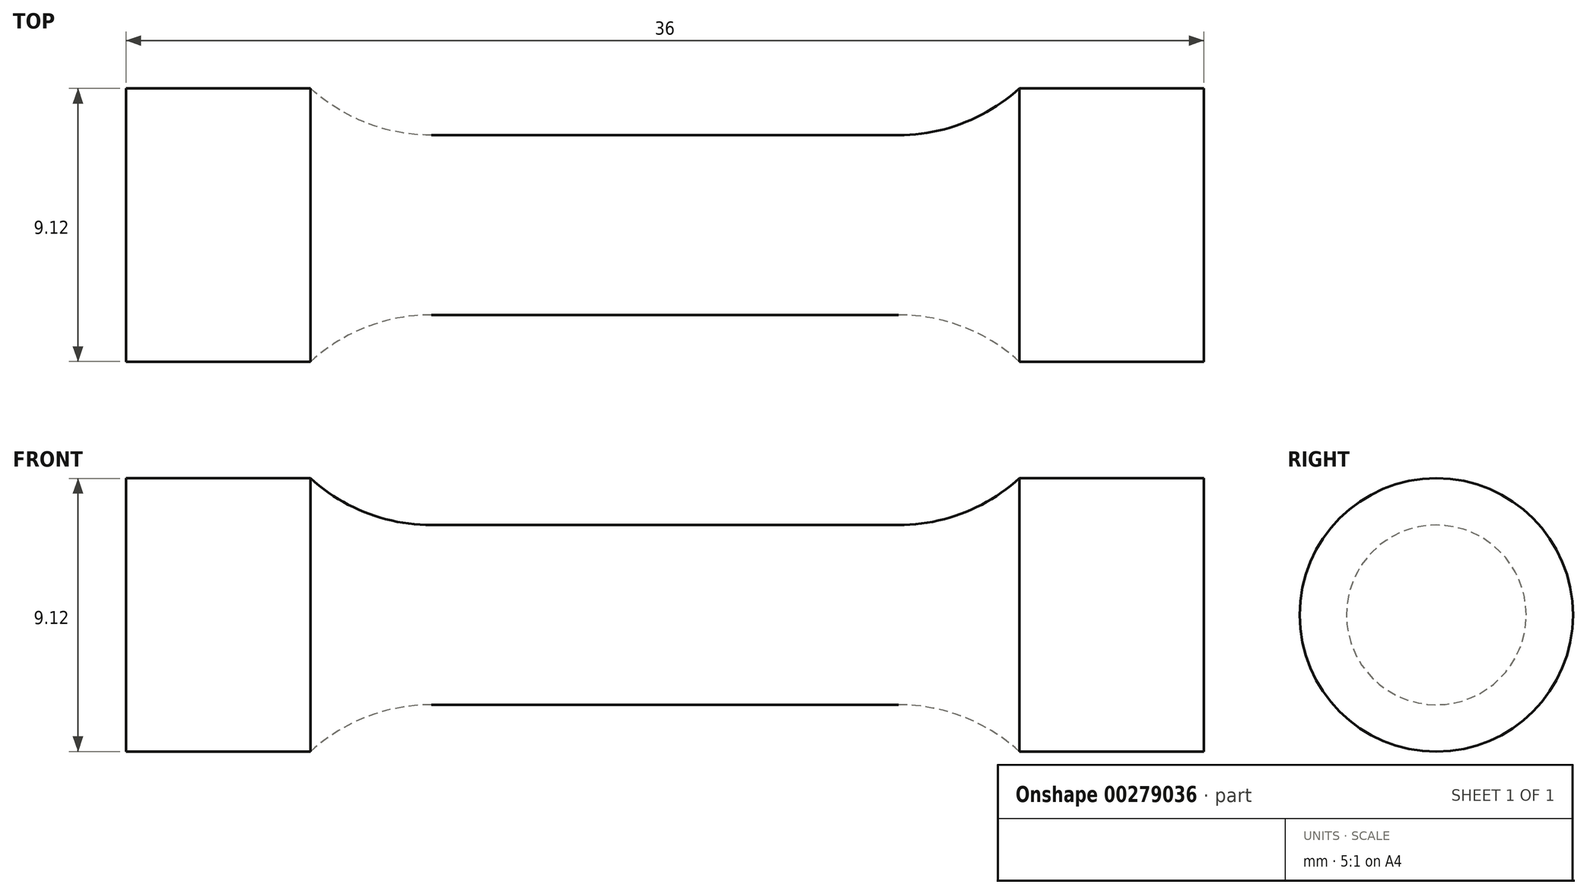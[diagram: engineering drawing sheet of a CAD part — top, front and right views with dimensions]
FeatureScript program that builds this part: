
annotation { "Feature Type Name" : "Feature", "Feature Type Description" : "" }
export const myFeature = defineFeature(function(context is Context, id is Id, definition is map)
    precondition{}
    {
        {
            var Q0;
            Q0=qCreatedBy(makeId("Front.planeOp"),FACE);
            var sketch = newSketch(context, id + "F0", { "sketchPlane" : qUnion([Q0])});
            skLineSegment(sketch, "E0", {"start": v(0, 3) * mm, "end": v(7.8, 3) * mm});
            skArc(sketch, "E1", {"start": v(7.8, 3) * mm, "mid": v(9.96, 3.4) * mm, "end": v(11.84, 4.56) * mm});
            skLineSegment(sketch, "E2", {"start": v(11.84, 4.56) * mm, "end": v(18, 4.56) * mm});
            skLineSegment(sketch, "E3", {"start": v(18, 4.56) * mm, "end": v(18, 0) * mm});
            skLineSegment(sketch, "E4.MirrorCS", {"start": v(0, 3) * mm, "end": v(-7.8, 3) * mm});
            skLineSegment(sketch, "E5.MirrorCS", {"start": v(-18, 4.56) * mm, "end": v(-18, 0) * mm});
            skLineSegment(sketch, "E6.MirrorCS", {"start": v(-11.84, 4.56) * mm, "end": v(-18, 4.56) * mm});
            skArc(sketch, "E7.MirrorCS", {"start": v(-7.8, 3) * mm, "mid": v(-9.96, 3.4) * mm, "end": v(-11.84, 4.56) * mm});
            skLineSegment(sketch, "E8", {"start": v(-18, 0) * mm, "end": v(18, 0) * mm});
            skSolve(sketch);
        }
        {
            var Q0;
            Q0=makeQuery(id+"F0.imprint","IMPRINT",FACE,{"disambiguationData":[TD([[makeQuery(id+"F0.imprint","IMPRINT",EDGE,{"derivedFrom":sQuery(id+"F0.wireOp",EDGE,"E0")}),-1.0]])]});
            var Q1;
            Q1=sQuery(id+"F0.wireOp",EDGE,"E8");
            revolve(context, id + "F1", {"entities" : qUnion([Q0]), "axis" : qUnion([Q1]), "revolveType" : RevolveType.FULL});
        }
    });
